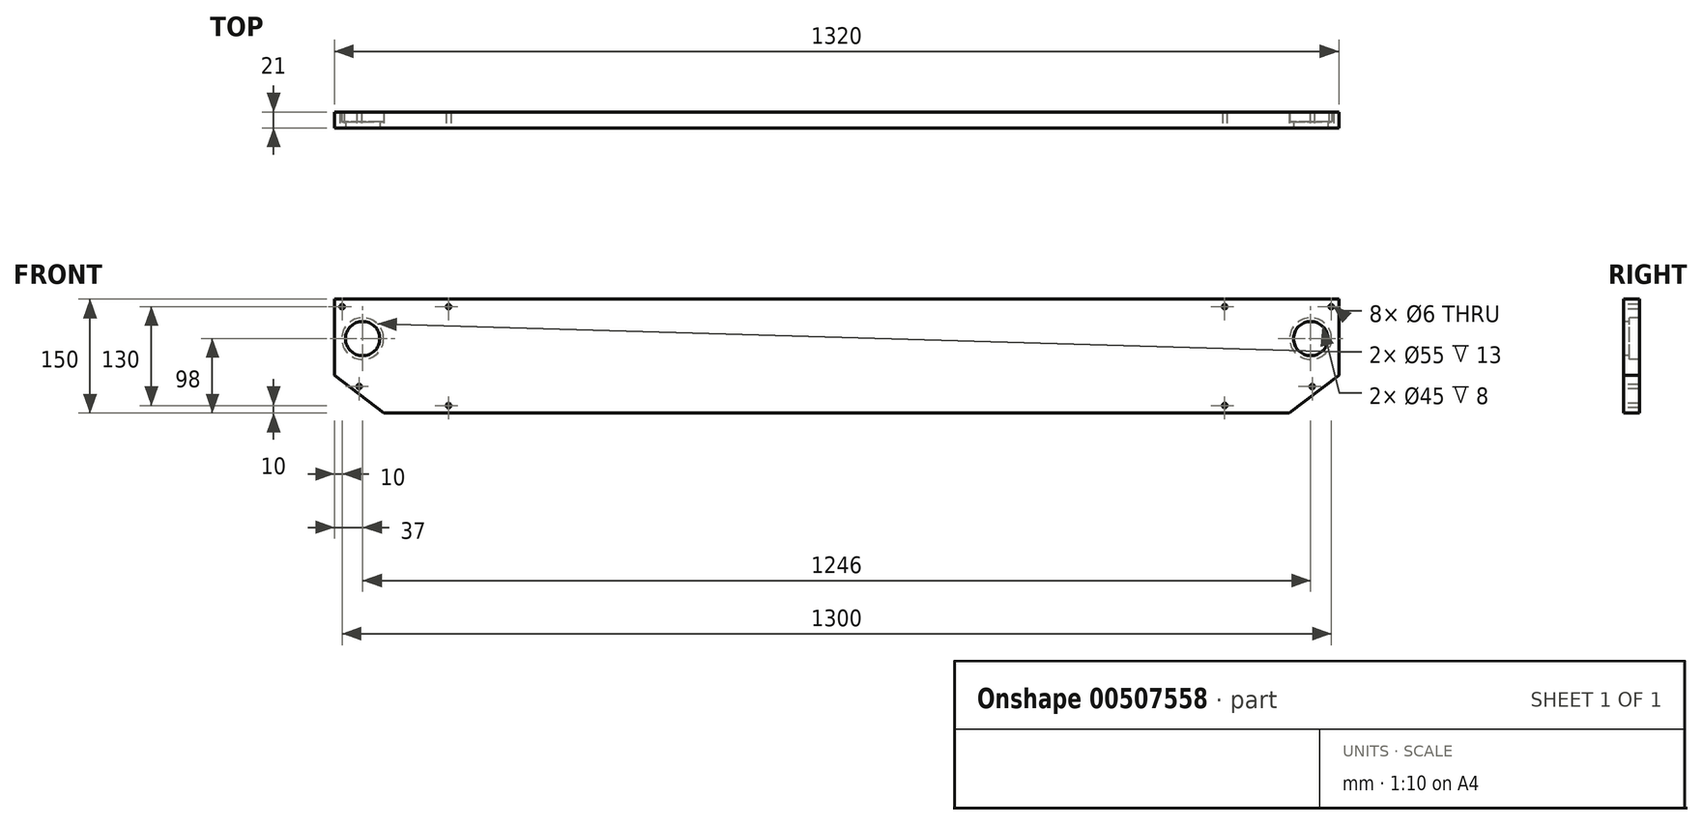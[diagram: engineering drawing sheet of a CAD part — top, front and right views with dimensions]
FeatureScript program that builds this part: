
annotation { "Feature Type Name" : "Feature", "Feature Type Description" : "" }
export const myFeature = defineFeature(function(context is Context, id is Id, definition is map)
    precondition{}
    {
        {
            var Q0;
            Q0=qCreatedBy(makeId("Front.planeOp"),FACE);
            var sketch = newSketch(context, id + "F0", { "sketchPlane" : qUnion([Q0])});
            skLineSegment(sketch, "E0.bottom", {"start": v(65, 0) * mm, "end": v(160, 0) * mm});
            skLineSegment(sketch, "E0.top", {"start": v(0, 150) * mm, "end": v(160, 150) * mm});
            skLineSegment(sketch, "E0.left", {"start": v(0, 50) * mm, "end": v(0, 150) * mm});
            skLineSegment(sketch, "E1.bottom", {"start": v(160, 0) * mm, "end": v(65, 0) * mm});
            skLineSegment(sketch, "E2.right", {"start": v(0, 50) * mm, "end": v(0, 120) * mm});
            skCircle(sketch, "E3", {"center": v(37, 98) * mm, "radius": 27.5 * mm});
            skLineSegment(sketch, "E4", {"start": v(65, 0) * mm, "end": v(0, 50) * mm});
            skPoint(sketch, "E5.centerSnap0", {"position": v(37, 120) * mm});
            skLineSegment(sketch, "E6.left", {"start": v(1320, 50) * mm, "end": v(1320, 150) * mm});
            skLineSegment(sketch, "E7.MirrorCS", {"start": v(160, 0) * mm, "end": v(1255, 0) * mm});
            skLineSegment(sketch, "E8.MirrorCS", {"start": v(1255, 0) * mm, "end": v(1320, 50) * mm});
            skLineSegment(sketch, "E9.MirrorCS", {"start": v(1320, 150) * mm, "end": v(160, 150) * mm});
            skCircle(sketch, "E10", {"center": v(1283, 98) * mm, "radius": 27.5 * mm});
            skCircle(sketch, "E11", {"center": v(10, 140) * mm, "radius": 3 * mm});
            skCircle(sketch, "E12", {"center": v(150, 140) * mm, "radius": 3 * mm});
            skCircle(sketch, "E13", {"center": v(150, 10) * mm, "radius": 3 * mm});
            skCircle(sketch, "E14", {"center": v(32.5, 35) * mm, "radius": 3 * mm});
            skCircle(sketch, "E15", {"center": v(1170, 10) * mm, "radius": 3 * mm});
            skCircle(sketch, "E16", {"center": v(1170, 140) * mm, "radius": 3 * mm});
            skCircle(sketch, "E17", {"center": v(1310, 140) * mm, "radius": 3 * mm});
            skCircle(sketch, "E18", {"center": v(1285, 35) * mm, "radius": 3 * mm});
            skSolve(sketch);
        }
        {
            var Q0;
            Q0=makeQuery(id+"F0.imprint","IMPRINT",FACE,{"disambiguationData":[TD([[makeQuery(id+"F0.imprint","IMPRINT",EDGE,{"derivedFrom":sQuery(id+"F0.wireOp",EDGE,"E0.right")}),-1.0]])]});
            var Q1;
            Q1=makeQuery(id+"F0.imprint","IMPRINT",FACE,{"disambiguationData":[TD([[makeQuery(id+"F0.imprint","IMPRINT",EDGE,{"derivedFrom":sQuery(id+"F0.wireOp",EDGE,"E0.top")}),-1.0]])]});
            var Q2;
            Q2=makeQuery(id+"F0.imprint","IMPRINT",FACE,{"disambiguationData":[TD([[makeQuery(id+"F0.imprint","IMPRINT",EDGE,{"derivedFrom":sQuery(id+"F0.wireOp",EDGE,"E1.bottom")}),-1.0]])]});
            var Q3;
            Q3=makeQuery(id+"F0.imprint","IMPRINT",FACE,{"disambiguationData":[TD([[makeQuery(id+"F0.imprint","IMPRINT",EDGE,{"derivedFrom":sQuery(id+"F0.wireOp",EDGE,"E1.right")}),1.0]])]});
            var Q4;
            {var subQ7=sQuery(id+"F0.wireOp",EDGE,"E2.bottom");Q4=makeQuery(id+"F0.imprint","IMPRINT",FACE,{"disambiguationData":[TD([[makeQuery(id+"F0.imprint","IMPRINT",EDGE,{"derivedFrom":subQ7}),-1.0]])]});}
            var Q5;
            {var subQ0=sQuery(id+"F0.wireOp",EDGE,"16491a0d-8a7a-4e64-846d-bfac5cd48ed5");Q5=makeQuery(id+"F0.imprint","IMPRINT",FACE,{"disambiguationData":[TD([[makeQuery(id+"F0.imprint","IMPRINT",EDGE,{"derivedFrom":subQ0}),1.0]])]});}
            var Q6;
            Q6=makeQuery(id+"F0.imprint","IMPRINT",FACE,{"disambiguationData":[TD([[makeQuery(id+"F0.imprint","IMPRINT",EDGE,{"derivedFrom":sQuery(id+"F0.wireOp",EDGE,"2f538665-d4e9-4531-9002-c1bc30a6b329")}),1.0]])]});
            var Q7;
            {var subQ4=sQuery(id+"F0.wireOp",EDGE,"E2.left");var subQ5=makeQuery(id+"F0.imprint","INTERSECT",VERTEX,{"derivedFrom":[sQuery(id+"F0.wireOp",EDGE,"E1.top"),subQ4]});Q7=makeQuery(id+"F0.imprint","IMPRINT",FACE,{"disambiguationData":[TD([[makeQuery(id+"F0.imprint","IMPRINT",EDGE,{"disambiguationData":[TD([[subQ5,1.0]])],"derivedFrom":subQ4}),1.0]])]});}
            var Q8;
            {var subQ0=sQuery(id+"F0.wireOp",EDGE,"E2.left");var subQ1=sQuery(id+"F0.wireOp",EDGE,"E1.top");var subQ2=makeQuery(id+"F0.imprint","INTERSECT",VERTEX,{"derivedFrom":[subQ1,subQ0]});Q8=makeQuery(id+"F0.imprint","IMPRINT",FACE,{"disambiguationData":[TD([[makeQuery(id+"F0.imprint","IMPRINT",EDGE,{"disambiguationData":[TD([[subQ2,1.0]])],"derivedFrom":subQ1}),1.0]])]});}
            var Q9;
            {var subQ0=sQuery(id+"F0.wireOp",EDGE,"E2.left");var subQ1=sQuery(id+"F0.wireOp",EDGE,"E1.top");var subQ2=makeQuery(id+"F0.imprint","INTERSECT",VERTEX,{"derivedFrom":[subQ1,subQ0]});Q9=makeQuery(id+"F0.imprint","IMPRINT",FACE,{"disambiguationData":[TD([[makeQuery(id+"F0.imprint","IMPRINT",EDGE,{"disambiguationData":[TD([[subQ2,1.0]])],"derivedFrom":subQ1}),-1.0]])]});}
            var Q10;
            {var subQ0=sQuery(id+"F0.wireOp",EDGE,"bc124edc-306a-48b3-9e66-1444ea52f558.bottom");Q10=makeQuery(id+"F0.imprint","IMPRINT",FACE,{"disambiguationData":[TD([[makeQuery(id+"F0.imprint","IMPRINT",EDGE,{"derivedFrom":subQ0}),1.0]])]});}
            var Q11;
            {var subQ0=sQuery(id+"F0.wireOp",EDGE,"6a3c666f-9f25-403a-8e2f-4488a8930037");var subQ1=sQuery(id+"F0.wireOp",EDGE,"E3");var subQ2=makeQuery(id+"F0.imprint","INTERSECT",VERTEX,{"disambiguationData":[OD(0.0)],"derivedFrom":[subQ1,subQ0]});Q11=makeQuery(id+"F0.imprint","IMPRINT",FACE,{"disambiguationData":[TD([[makeQuery(id+"F0.imprint","IMPRINT",EDGE,{"disambiguationData":[TD([[subQ2,-1.0]])],"derivedFrom":subQ1}),-1.0]])]});}
            extrude(context, id + "F1", {"entities" : qUnion([Q0, Q1, Q2, Q3, Q4, Q5, Q6, Q7, Q8, Q9, Q10, Q11]), "oppositeDirection" : true, "depth" : 21 * mm, "offsetDistance" : 25 * mm});
        }
        {
            var Q0;
            Q0=makeQuery(id+"F1.opExtrude","CAP_FACE",FACE,{"disambiguationData":[OSD([sQuery(id+"F0.wireOp",EDGE,"E0.top"),sQuery(id+"F0.wireOp",EDGE,"E0.left"),sQuery(id+"F0.wireOp",EDGE,"E1.bottom"),sQuery(id+"F0.wireOp",EDGE,"E2.right"),sQuery(id+"F0.wireOp",EDGE,"E3"),sQuery(id+"F0.wireOp",EDGE,"E4"),sQuery(id+"F0.wireOp",EDGE,"E6.left"),sQuery(id+"F0.wireOp",EDGE,"E7.MirrorCS"),sQuery(id+"F0.wireOp",EDGE,"E8.MirrorCS"),sQuery(id+"F0.wireOp",EDGE,"E9.MirrorCS"),sQuery(id+"F0.wireOp",EDGE,"E10"),sQuery(id+"F0.wireOp",EDGE,"E11"),sQuery(id+"F0.wireOp",EDGE,"E12"),sQuery(id+"F0.wireOp",EDGE,"E13"),sQuery(id+"F0.wireOp",EDGE,"E14"),sQuery(id+"F0.wireOp",EDGE,"E15"),sQuery(id+"F0.wireOp",EDGE,"E16"),sQuery(id+"F0.wireOp",EDGE,"E17"),sQuery(id+"F0.wireOp",EDGE,"E18")])],"isStart":true});
            var sketch = newSketch(context, id + "F2", { "sketchPlane" : qUnion([Q0])});
            skCircle(sketch, "E19", {"center": v(37, 98) * mm, "radius": 22.5 * mm});
            skCircle(sketch, "E20", {"center": v(1283, 98) * mm, "radius": 22.5 * mm});
            skSolve(sketch);
        }
        {
            var Q0;
            Q0=makeQuery(id+"F2.imprint","IMPRINT",FACE,{"disambiguationData":[TD([[makeQuery(id+"F2.imprint","IMPRINT",EDGE,{"derivedFrom":sQuery(id+"F2.wireOp",EDGE,"E20")}),-1.0]])]});
            var Q1;
            Q1=makeQuery(id+"F2.imprint","IMPRINT",FACE,{"disambiguationData":[TD([[makeQuery(id+"F2.imprint","IMPRINT",EDGE,{"derivedFrom":sQuery(id+"F2.wireOp",EDGE,"E19")}),-1.0]])]});
            extrude(context, id + "F3", {"entities" : qUnion([Q0, Q1]), "operationType" : NewBodyOperationType.ADD, "oppositeDirection" : true, "depth" : 8 * mm, "offsetDistance" : 25 * mm});
        }
    });
